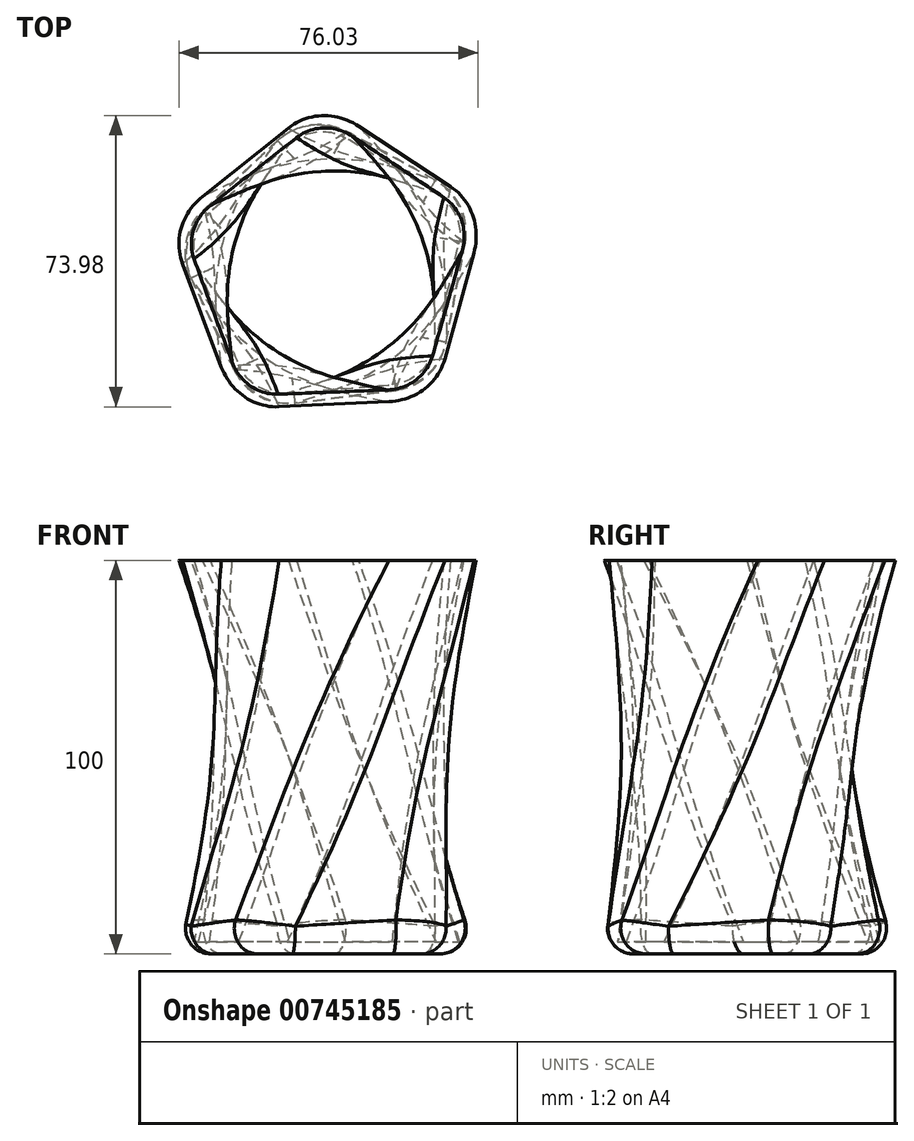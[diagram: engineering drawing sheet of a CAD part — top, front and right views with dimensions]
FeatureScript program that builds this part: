
annotation { "Feature Type Name" : "Feature", "Feature Type Description" : "" }
export const myFeature = defineFeature(function(context is Context, id is Id, definition is map)
    precondition{}
    {
        {
            var Q0;
            Q0=qCreatedBy(makeId("Top.planeOp"),FACE);
            cPlane(context, id + "F0", {"entities" : qUnion([Q0]), "cplaneType" : CPlaneType.OFFSET, "offset" : 100 * mm, "width" : 150 * mm, "height" : 150 * mm});
        }
        {
            var Q0;
            Q0=qCreatedBy(makeId("Top.planeOp"),FACE);
            var sketch = newSketch(context, id + "F1", { "sketchPlane" : qUnion([Q0])});
            skCircle(sketch, "E0.cCircle", {"center": v(0, 0) * mm, "radius": 34.4 * mm, "construction": true});
            skLineSegment(sketch, "E0.0", {"start": v(39.8, 15) * mm, "end": v(26.56, -33.22) * mm});
            skLineSegment(sketch, "E0.1", {"start": v(26.56, -33.22) * mm, "end": v(-23.39, -35.52) * mm});
            skLineSegment(sketch, "E0.2", {"start": v(-23.39, -35.52) * mm, "end": v(-41.01, 11.27) * mm});
            skLineSegment(sketch, "E0.3", {"start": v(-41.01, 11.27) * mm, "end": v(-1.96, 42.49) * mm});
            skLineSegment(sketch, "E0.4", {"start": v(-1.96, 42.49) * mm, "end": v(39.8, 15) * mm});
            skPoint(sketch, "E0.0.midPoint", {"position": v(33.18, -9.12) * mm});
            skSolve(sketch);
        }
        {
            var Q0;
            Q0=qCreatedBy(id+"F0.planeOp",FACE);
            var sketch = newSketch(context, id + "F2", { "sketchPlane" : qUnion([Q0])});
            skLineSegment(sketch, "E1.0", {"start": v(-23.39, -35.52) * mm, "end": v(-41.01, 11.27) * mm});
            skLineSegment(sketch, "E1.1", {"start": v(26.56, -33.22) * mm, "end": v(-23.39, -35.52) * mm});
            skLineSegment(sketch, "E1.2", {"start": v(39.8, 15) * mm, "end": v(26.56, -33.22) * mm});
            skLineSegment(sketch, "E1.3", {"start": v(-1.96, 42.49) * mm, "end": v(39.8, 15) * mm});
            skLineSegment(sketch, "E1.4", {"start": v(-41.01, 11.27) * mm, "end": v(-1.96, 42.49) * mm});
            skSolve(sketch);
        }
        {
            var Q0;
            Q0=makeQuery(id+"F1.imprint","IMPRINT",FACE,{"disambiguationData":[TD([[makeQuery(id+"F1.imprint","IMPRINT",EDGE,{"derivedFrom":sQuery(id+"F1.wireOp",EDGE,"E0.0")}),-1.0]])]});
            var Q1;
            Q1=makeQuery(id+"F2.imprint","IMPRINT",FACE,{"disambiguationData":[TD([[makeQuery(id+"F2.imprint","IMPRINT",EDGE,{"derivedFrom":sQuery(id+"F2.wireOp",EDGE,"E1.0")}),-1.0]])]});
            var Q2;
            Q2=sQuery(id+"F2.wireOp",VERTEX,"E1.2.end");
            var Q3;
            Q3=sQuery(id+"F1.wireOp",VERTEX,"E0.2.start");
            loft(context, id + "F3", {"sheetProfilesArray" : [{ "sheetProfileEntities" : qUnion([Q0]) }, { "sheetProfileEntities" : qUnion([Q1]) }], "matchConnections" : true, "connections" : [{ "connectionEntities" : qUnion([Q2, Q3]), "connectionEdgeQueries" : qUnion([]), "connectionEdgeParameters" : [] }]});
        }
        {
            var Q0;
            Q0=makeQuery(id+"F3.opLoft","SWEPT_EDGE",EDGE,{"disambiguationData":[OSD([sQuery(id+"F1.wireOp",EDGE,"E0.3"),sQuery(id+"F1.wireOp",EDGE,"E0.4"),sQuery(id+"F2.wireOp",EDGE,"E1.0"),sQuery(id+"F2.wireOp",EDGE,"E1.4")])]});
            var Q1;
            Q1=makeQuery(id+"F3.opLoft","SWEPT_EDGE",EDGE,{"disambiguationData":[OSD([sQuery(id+"F1.wireOp",EDGE,"E0.2"),sQuery(id+"F1.wireOp",EDGE,"E0.3"),sQuery(id+"F2.wireOp",EDGE,"E1.0"),sQuery(id+"F2.wireOp",EDGE,"E1.1")])]});
            var Q2;
            Q2=makeQuery(id+"F3.opLoft","SWEPT_EDGE",EDGE,{"disambiguationData":[OSD([sQuery(id+"F1.wireOp",EDGE,"E0.1"),sQuery(id+"F1.wireOp",EDGE,"E0.2"),sQuery(id+"F2.wireOp",EDGE,"E1.1"),sQuery(id+"F2.wireOp",EDGE,"E1.2")])]});
            var Q3;
            Q3=makeQuery(id+"F3.opLoft","SWEPT_EDGE",EDGE,{"disambiguationData":[OSD([sQuery(id+"F1.wireOp",EDGE,"E0.0"),sQuery(id+"F1.wireOp",EDGE,"E0.1"),sQuery(id+"F2.wireOp",EDGE,"E1.2"),sQuery(id+"F2.wireOp",EDGE,"E1.3")])]});
            var Q4;
            Q4=makeQuery(id+"F3.opLoft","SWEPT_EDGE",EDGE,{"disambiguationData":[OSD([sQuery(id+"F1.wireOp",EDGE,"E0.0"),sQuery(id+"F1.wireOp",EDGE,"E0.4"),sQuery(id+"F2.wireOp",EDGE,"E1.3"),sQuery(id+"F2.wireOp",EDGE,"E1.4")])]});
            fillet(context, id + "F4", {"entities" : qUnion([Q0, Q1, Q2, Q3, Q4]), "radius" : 15 * mm, "tangentPropagation" : true, "allowEdgeOverflow" : false});
        }
        {
            var Q0;
            Q0=makeQuery(id+"F3.opLoft","CAP_FACE",FACE,{"disambiguationData":[OSD([makeQuery(id+"F2.imprint","IMPRINT",FACE,{"disambiguationData":[TD([[makeQuery(id+"F2.imprint","IMPRINT",EDGE,{"derivedFrom":sQuery(id+"F2.wireOp",EDGE,"E1.0")}),-1.0]])]})])],"isStart":true});
            shell(context, id + "F5", {"entities" : qUnion([Q0]), "thickness" : 3 * mm});
        }
        {
            var Q0;
            Q0=makeQuery(id+"F3.opLoft","CAP_FACE",FACE,{"disambiguationData":[OSD([makeQuery(id+"F1.imprint","IMPRINT",FACE,{"disambiguationData":[TD([[makeQuery(id+"F1.imprint","IMPRINT",EDGE,{"derivedFrom":sQuery(id+"F1.wireOp",EDGE,"E0.0")}),-1.0]])]})])],"isStart":true});
            fillet(context, id + "F6", {"entities" : qUnion([Q0]), "radius" : 6.5 * mm, "tangentPropagation" : true, "allowEdgeOverflow" : false});
        }
    });
